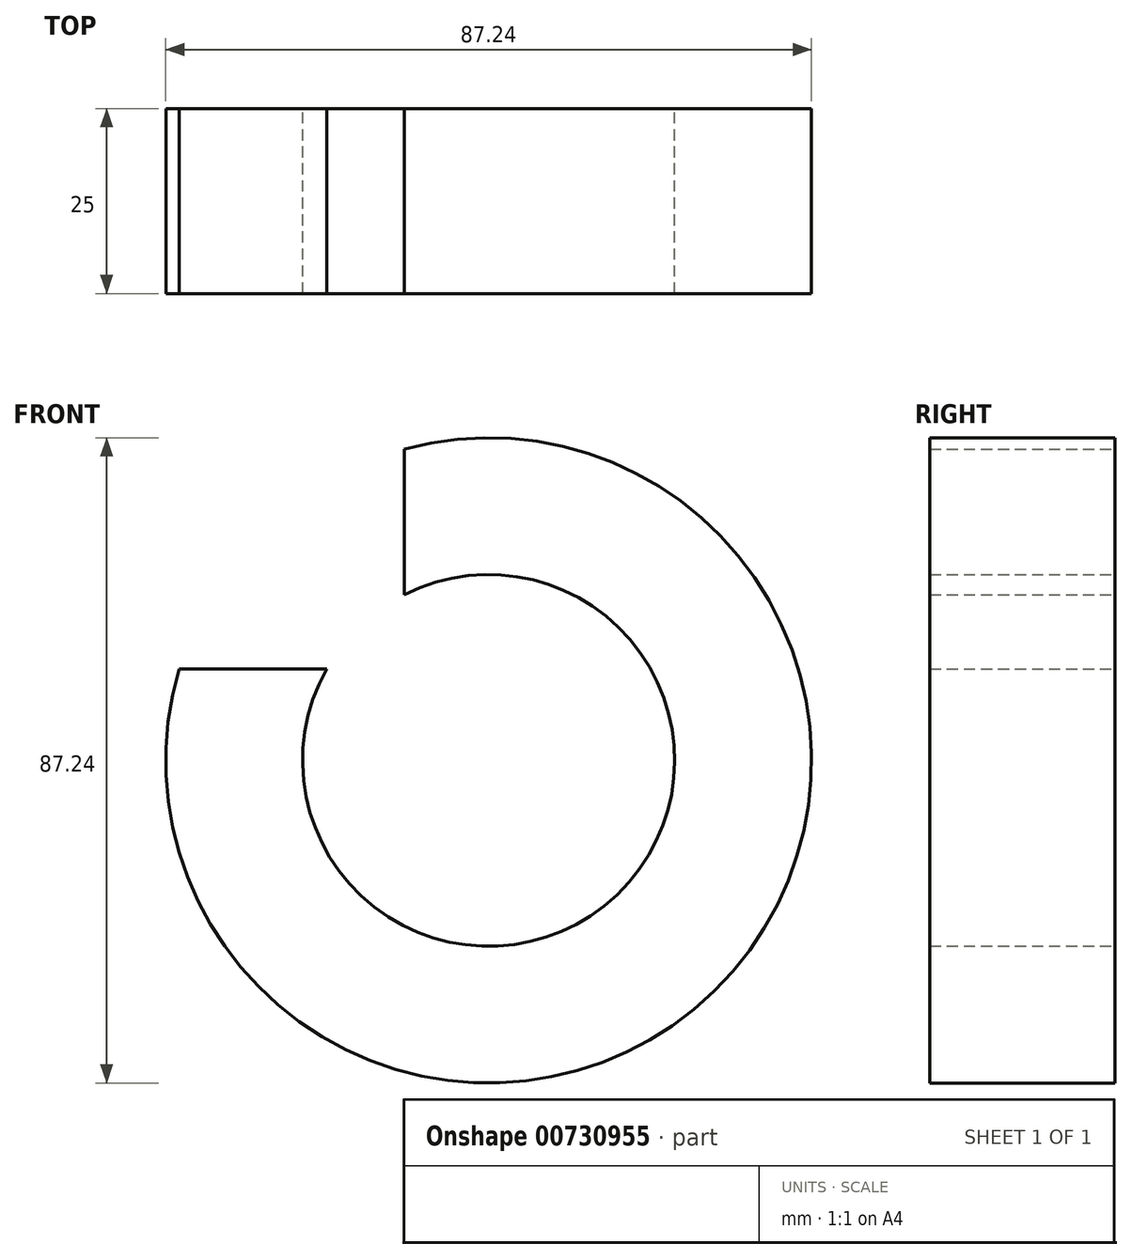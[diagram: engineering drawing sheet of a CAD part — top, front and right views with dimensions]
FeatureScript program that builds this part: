
annotation { "Feature Type Name" : "Feature", "Feature Type Description" : "" }
export const myFeature = defineFeature(function(context is Context, id is Id, definition is map)
    precondition{}
    {
        {
            var Q0;
            Q0=qCreatedBy(makeId("Front.planeOp"),FACE);
            var sketch = newSketch(context, id + "F0", { "sketchPlane" : qUnion([Q0])});
            skCircle(sketch, "E0", {"center": v(0, 0) * mm, "radius": 43.62 * mm});
            skCircle(sketch, "E1", {"center": v(0, 0) * mm, "radius": 25.13 * mm});
            skSolve(sketch);
        }
        {
            var Q0;
            Q0 = qSketchRegion(id + "F0", true);
            extrude(context, id + "F1", {"entities" : qUnion([Q0]), "depth" : 25 * mm, "offsetDistance" : 25.4 * mm});
        }
        {
            var Q0;
            Q0=qCreatedBy(makeId("Front.planeOp"),FACE);
            var sketch = newSketch(context, id + "F2", { "sketchPlane" : qUnion([Q0])});
            skLineSegment(sketch, "E2.bottom", {"start": v(-11.4, 12.4) * mm, "end": v(-52, 12.4) * mm});
            skLineSegment(sketch, "E2.top", {"start": v(-11.4, 43.82) * mm, "end": v(-52, 43.82) * mm});
            skLineSegment(sketch, "E2.left", {"start": v(-11.4, 12.4) * mm, "end": v(-11.4, 43.82) * mm});
            skLineSegment(sketch, "E2.right", {"start": v(-52, 12.4) * mm, "end": v(-52, 43.82) * mm});
            skSolve(sketch);
        }
        {
            var Q0;
            Q0 = qSketchRegion(id + "F2", true);
            extrude(context, id + "F3", {"entities" : qUnion([Q0]), "operationType" : NewBodyOperationType.REMOVE, "depth" : 25 * mm, "offsetDistance" : 25 * mm});
        }
    });
